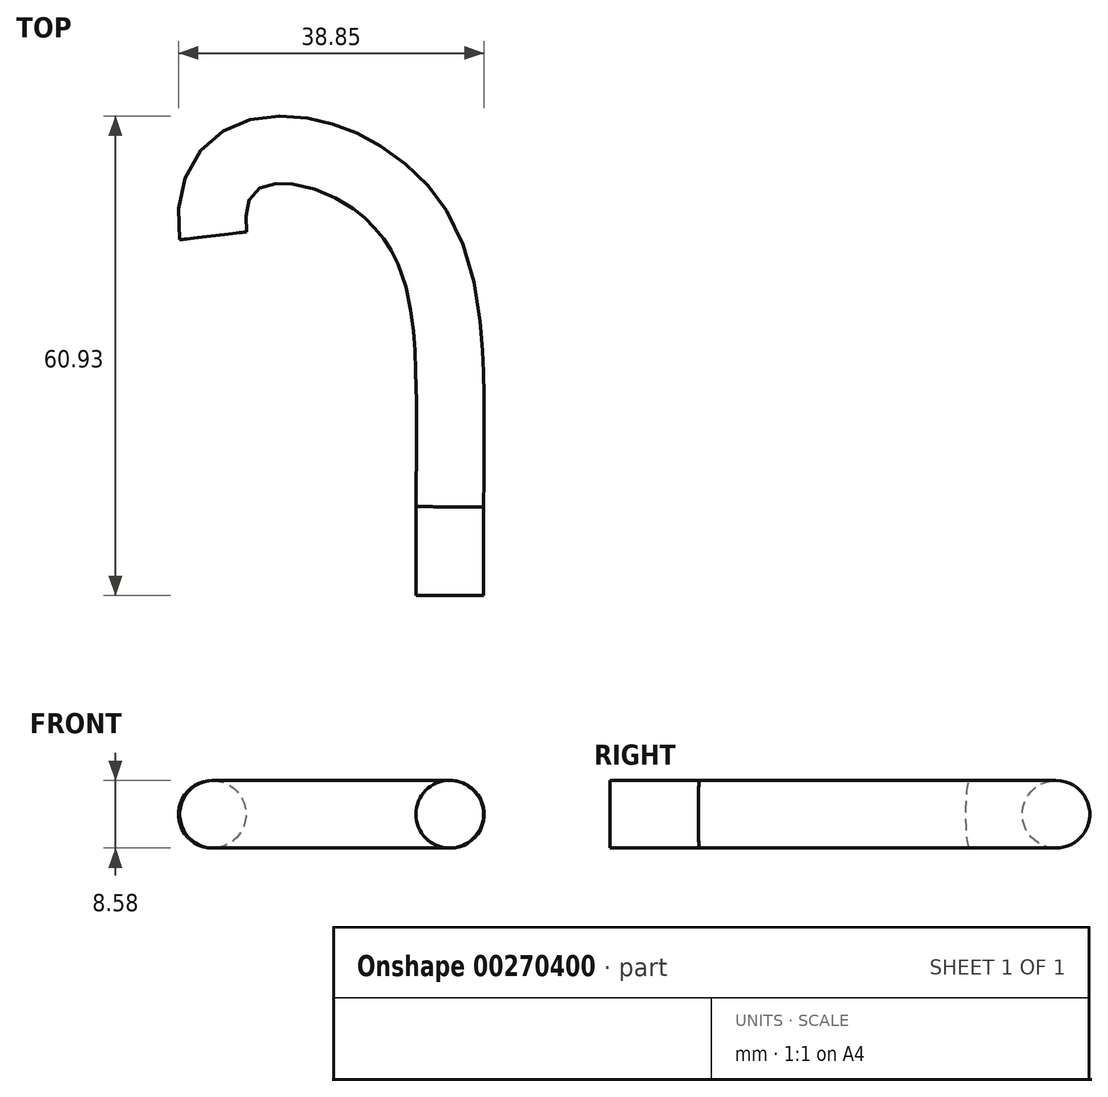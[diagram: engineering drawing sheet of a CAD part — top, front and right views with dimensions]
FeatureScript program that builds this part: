
annotation { "Feature Type Name" : "Feature", "Feature Type Description" : "" }
export const myFeature = defineFeature(function(context is Context, id is Id, definition is map)
    precondition{}
    {
        {
            var Q0;
            Q0=qCreatedBy(makeId("Top.planeOp"),FACE);
            var sketch = newSketch(context, id + "F0", { "sketchPlane" : qUnion([Q0])});
            skLineSegment(sketch, "E0", {"start": v(0, 0) * mm, "end": v(0, 11.26) * mm});
            skFitSpline(sketch, "E1", {"points": [v(0, 11.26) * mm, v(0, 28) * mm, v(-4.5, 47.3) * mm, v(-21.24, 56.64) * mm, v(-30.04, 45.7) * mm], "startDerivative": vector(0.85, 66.77) * mm, "endDerivative": vector(12.8, -108.55) * mm});
            skSolve(sketch);
        }
        {
            var Q0;
            Q0=qCreatedBy(makeId("Front.planeOp"),FACE);
            var sketch = newSketch(context, id + "F1", { "sketchPlane" : qUnion([Q0])});
            skCircle(sketch, "E2", {"center": v(0, 0) * mm, "radius": 4.3 * mm});
            skSolve(sketch);
        }
        {
            var Q0;
            Q0=makeQuery(id+"F1.imprint","IMPRINT",FACE,{"disambiguationData":[TD([[makeQuery(id+"F1.imprint","IMPRINT",EDGE,{"derivedFrom":sQuery(id+"F1.wireOp",EDGE,"E2")}),1.0]])]});
            var Q1;
            Q1=sQuery(id+"F0.wireOp",EDGE,"E0");
            var Q2;
            Q2=sQuery(id+"F0.wireOp",EDGE,"E1");
            sweep(context, id + "F2", {"profiles" : qUnion([Q0]), "path" : qUnion([Q1, Q2])});
        }
    });
